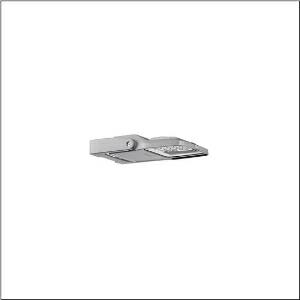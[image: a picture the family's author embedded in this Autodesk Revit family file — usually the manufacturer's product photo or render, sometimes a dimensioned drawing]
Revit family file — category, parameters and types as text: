
# Revit family: floodlight_fl_21_iq_micro___pl43_5xa7762a2a2a_df73
name_source: partatom
category: Lighting Fixtures
units: mm (PartAtom-declared; Revit-internal decimal feet)

## family parameters
Cut with Voids When Loaded = No
Host = Face
Light Source = No
Part Type = Normal
Room Calculation Point = No
Round Connector Dimension = Use Diameter
Shared = No

## types (1)
- --- (1 x LED, 3040 lm, 23.1 W, 3000K)
    Apparent Load = 23 VA
    CIE Flux Codes = 29 80 99 100 100
    Color Rendering = 70
    Color Temperature = 3000K
    Default Elevation = 1800 mm
    Description = Floodlight FL 21 iQ micro, floodlight, primary light control with lens, of PMMA, primary optical cover: protective disc, of toughened safety glass, transparent, light distribution: PL43, light emission: direct distribution, installation type: surface-mounted, LED, High Power LED, rated luminous flux: 3.040lm, luminous efficacy: 132lm/W, light colour: 730, colour temperature: 3000K, control gear: iQ Street-Remote/DALI, control: Auto-Match, Temp-Guard, Night-Set, Smart-Wire, Desk-Remote (wireless, voltage-free reading and setting of iQ features in the workshop via application-optimized NFC function/RFID function), optimised constant luminous flux control (CLO 2.0), Street-Remote, with terminal, 6-pole, mains connection: 220..240V, AC, 50/60Hz, start of lifetime: 23W, end of service life: 24W, reduction: 11W, luminaire housing, of diecast aluminium, powder-coated, Siteco® metallic grey (DB 702S), corrosivity category C5 mid according to DIN EN ISO 12944, suitable for swimming pools, chlorine-resistant, sealing non-destructively replaceable, design bracket, of diecast aluminium, powder-coated, Siteco® metallic grey (DB 702S), protection rating (complete): IP66, insulation class (complete): insulation class II (safety insulation), certification: CE, ENEC, VDE, protection symbol: D, impact resistance: IK07, permissible operating ambient temperature: -40..+40°C, permissible operating ambient temperature for outdoor applications: -40..+50°C, standard: DIN EN 12944, LABS conformity tested according to VDMA 24364:2018-05, packaging unit: 1 piece

Light Distribution: PL43
    Height = 65 mm
    Lamp = 1 x LED
    Lamp Light Flux = 3040 lm
    Lamp Power = 23.1 W
    Lamp count = 1
    Length = 312 mm
    Luminous efficacy = 132 lm/W
    Manufacturer = Siteco
    ModVariant = No
    Model = 5XA7762A2A2A
    Mounting Place = Wall
    Mounting Type = Surface mounted
    Number of Poles = 1
    OnlyDefault = Yes
    Power Factor = 1
    Product Name = Floodlight FL 21 iQ micro | PL43
    Product group = floodlight | wall mounted
    ProductGroupID = 2001
    Protection Class = Protection class II
    Protection Degree = IP 66
    RLX_Detail_Level = 1
    RLX_Emergency_Light_Flux = 0 lm
    RLX_Emergency_Type = 0
    RLX_Emergency_Type_DB = No
    RlxData = <blob elided: 97425 chars, md5=f64d4788>
    Socket = socket
    Standby Power = 0 W
    System Light Flux = 3040 lm
    System Power = 23 W
    Type Comments = factory setting: luminous flux: 100 % | dim-lin: 254 | 455 mA
    Type Image = l_1006878.jpg
    URL = http://relux.com
    VarID = @adj_176612
    Voltage = 0 V
    Weight = 0.00 kg
    Width = 230 mm

## geometry (parser evidence)
native form markers: Blend x4, Sweep x10
no freeform markers — native parametric forms only
